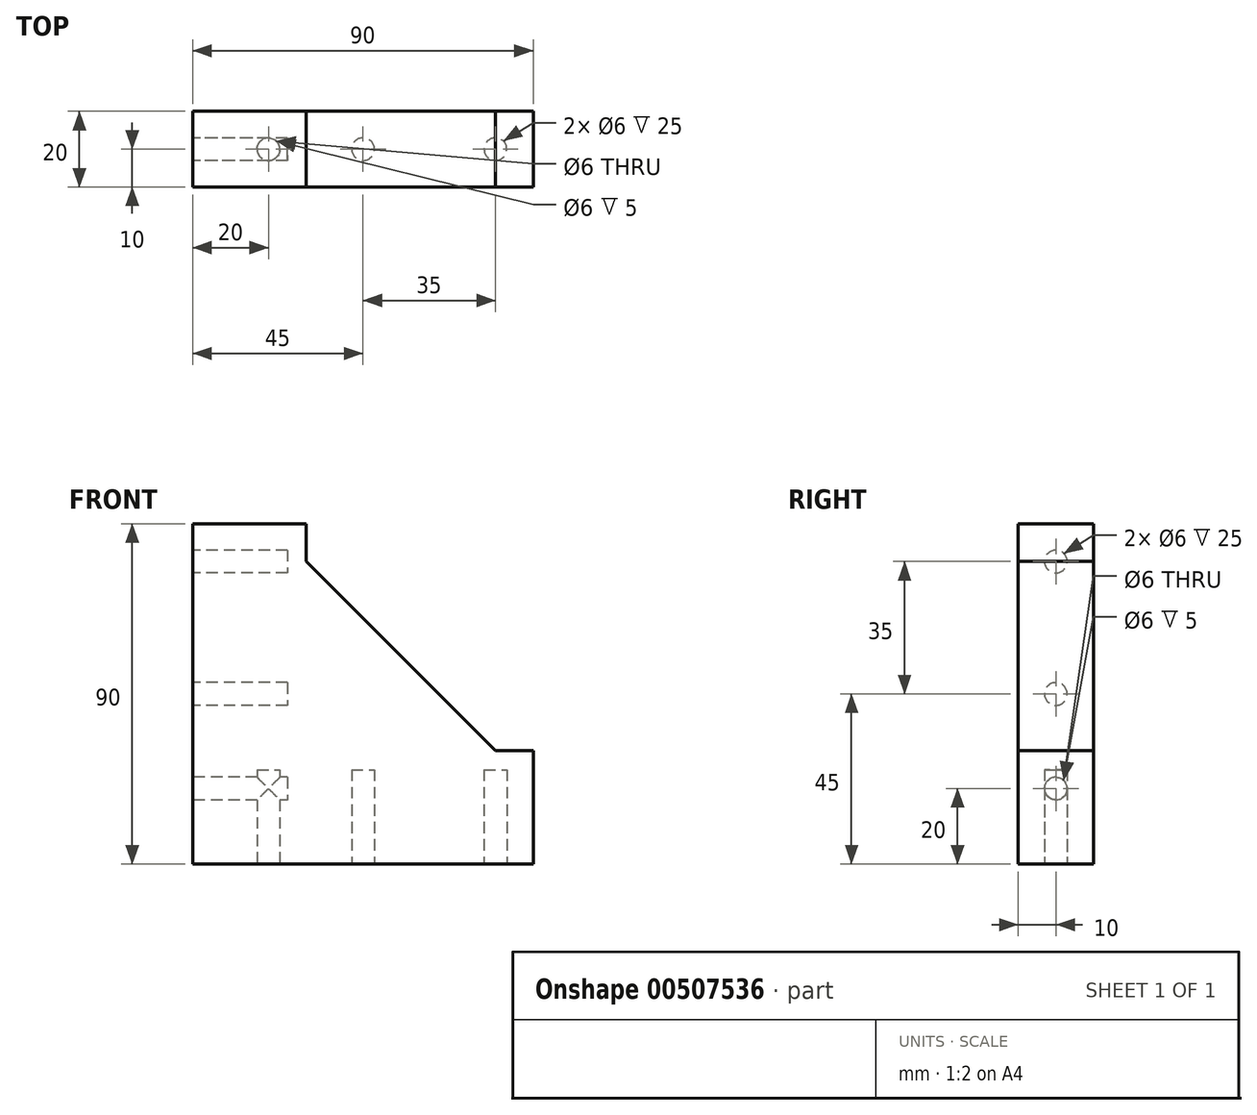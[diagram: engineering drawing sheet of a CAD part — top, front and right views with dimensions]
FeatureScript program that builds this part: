
annotation { "Feature Type Name" : "Feature", "Feature Type Description" : "" }
export const myFeature = defineFeature(function(context is Context, id is Id, definition is map)
    precondition{}
    {
        {
            var Q0;
            Q0=qCreatedBy(makeId("Front.planeOp"),FACE);
            var sketch = newSketch(context, id + "F0", { "sketchPlane" : qUnion([Q0])});
            skLineSegment(sketch, "E0", {"start": v(0, 0) * mm, "end": v(0, 90) * mm});
            skLineSegment(sketch, "E1", {"start": v(0, 90) * mm, "end": v(30, 90) * mm});
            skLineSegment(sketch, "E2", {"start": v(30, 90) * mm, "end": v(30, 80) * mm});
            skLineSegment(sketch, "E3", {"start": v(30, 80) * mm, "end": v(80, 30) * mm});
            skLineSegment(sketch, "E4", {"start": v(80, 30) * mm, "end": v(90, 30) * mm});
            skLineSegment(sketch, "E5", {"start": v(90, 30) * mm, "end": v(90, 0) * mm});
            skLineSegment(sketch, "E6", {"start": v(90, 0) * mm, "end": v(0, 0) * mm});
            skSolve(sketch);
        }
        {
            var Q0;
            Q0 = qSketchRegion(id + "F0", true);
            extrude(context, id + "F1", {"entities" : qUnion([Q0]), "depth" : 20 * mm});
        }
        {
            var Q0;
            Q0=makeQuery(id+"F1.opExtrude","SWEPT_FACE",FACE,{"disambiguationData":[OSD([sQuery(id+"F0.wireOp",EDGE,"E0")])]});
            var sketch = newSketch(context, id + "F2", { "sketchPlane" : qUnion([Q0])});
            skCircle(sketch, "E7", {"center": v(10, 20) * mm, "radius": 3 * mm});
            skCircle(sketch, "E8", {"center": v(10, 45) * mm, "radius": 3 * mm});
            skCircle(sketch, "E9", {"center": v(10, 80) * mm, "radius": 3 * mm});
            skSolve(sketch);
        }
        {
            var Q0;
            Q0 = qSketchRegion(id + "F2", true);
            extrude(context, id + "F3", {"entities" : qUnion([Q0]), "operationType" : NewBodyOperationType.REMOVE, "oppositeDirection" : true, "depth" : 25 * mm});
        }
        {
            var Q0;
            Q0=makeQuery(id+"F1.opExtrude","SWEPT_FACE",FACE,{"disambiguationData":[OSD([sQuery(id+"F0.wireOp",EDGE,"E6")])]});
            var sketch = newSketch(context, id + "F4", { "sketchPlane" : qUnion([Q0])});
            skCircle(sketch, "E10", {"center": v(20, 10) * mm, "radius": 3 * mm});
            skCircle(sketch, "E11", {"center": v(45, 10) * mm, "radius": 3 * mm});
            skCircle(sketch, "E12", {"center": v(80, 10) * mm, "radius": 3 * mm});
            skSolve(sketch);
        }
        {
            var Q0;
            Q0 = qSketchRegion(id + "F4", true);
            extrude(context, id + "F5", {"entities" : qUnion([Q0]), "operationType" : NewBodyOperationType.REMOVE, "oppositeDirection" : true, "depth" : 25 * mm});
        }
    });
